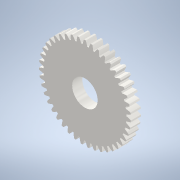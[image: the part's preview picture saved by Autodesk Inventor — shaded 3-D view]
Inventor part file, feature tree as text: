
AUTODESK INVENTOR PART (.ipt)
format: ipt  version: 2021 (Build 250183000, 183)  size: 330,240 bytes
history: native  units: mm (DEFAULTED — no unit token found)
features: plane x3, other x3, sketch x3, extrude x2
ambient origin geometry x8: Origin, YZ Plane, XZ Plane, XY Plane, X Axis, Y Axis, Z Axis, Center Point
bodies: Solid1 (feature_tree)
feature tree (11):
  extrude  "Extrusion1"  Depth=10.0mm TaperAngle=0.0deg
  plane  "Work Plane2"
  plane  "Work Plane8"
  plane  "Work Plane9"
  other  "Spur Gear"
  extrude  "Extrusion2"  Depth=10.0mm TaperAngle=0.0deg
  sketch  "Sketch1"  dims[d0=90.0mm d1=10.0mm d2=0.0mm]
  sketch  "Sketch2"  dims[d3=86.0mm d4=10.0mm d5=0.0mm]
  other  "Srf1"
  sketch  "Sketch3"  dims[d16=65.0mm d17=0.0mm d34=0.730603mm d39=0.0mm d41=0.0mm d43=65.0mm d46=65.0mm d47=0.0mm d48=0.0mm d49=25.0mm d50=10.0mm d51=0.0mm]
  other  "Pitch Diameter"
